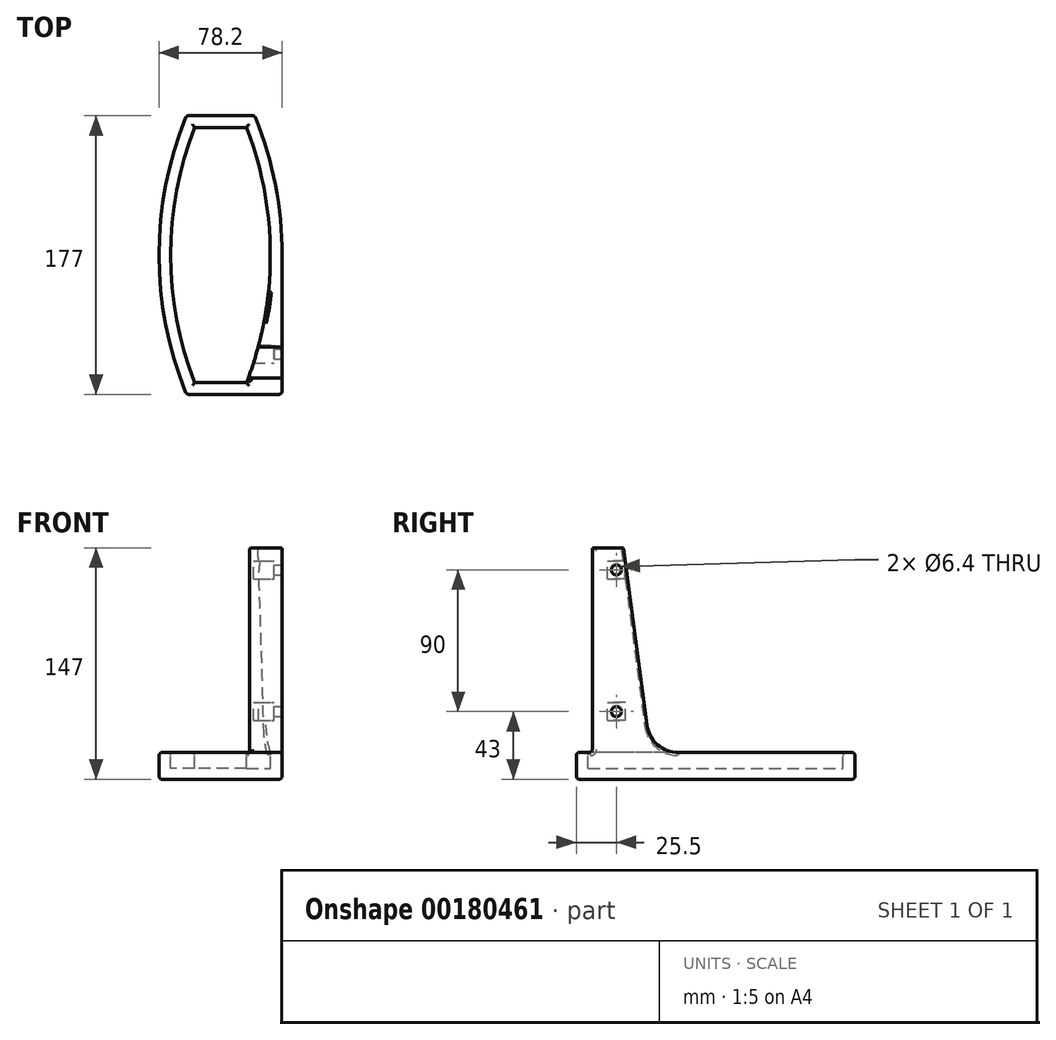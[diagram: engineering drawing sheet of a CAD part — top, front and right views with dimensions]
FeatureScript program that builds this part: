
annotation { "Feature Type Name" : "Feature", "Feature Type Description" : "" }
export const myFeature = defineFeature(function(context is Context, id is Id, definition is map)
    precondition{}
    {
        {
            var Q0;
            Q0=qCreatedBy(makeId("Top.planeOp"),FACE);
            var sketch = newSketch(context, id + "F0", { "sketchPlane" : qUnion([Q0])});
            skLineSegment(sketch, "E0.bottom", {"start": v(16.5, -81) * mm, "end": v(-16.5, -81) * mm});
            skLineSegment(sketch, "E0.top", {"start": v(16.5, 81) * mm, "end": v(-16.5, 81) * mm});
            skLineSegment(sketch, "E0.left", {"start": v(16.5, -81) * mm, "end": v(16.5, 81) * mm, "construction": true});
            skLineSegment(sketch, "E0.right", {"start": v(-16.5, -81) * mm, "end": v(-16.5, 81) * mm, "construction": true});
            skPoint(sketch, "E0.middle", {"position": v(0, 0) * mm});
            skArc(sketch, "E1", {"start": v(16.5, -81) * mm, "mid": v(31.6, 0) * mm, "end": v(16.5, 81) * mm});
            skArc(sketch, "E2", {"start": v(-16.5, 81) * mm, "mid": v(-31.6, 0) * mm, "end": v(-16.5, -81) * mm});
            skLineSegment(sketch, "E3", {"start": v(-31.6, 0) * mm, "end": v(31.6, 0) * mm, "construction": true});
            skSolve(sketch);
        }
        {
            var Q0;
            Q0=makeQuery(id+"F0.imprint","IMPRINT",FACE,{"disambiguationData":[TD([[makeQuery(id+"F0.imprint","IMPRINT",EDGE,{"derivedFrom":sQuery(id+"F0.wireOp",EDGE,"E0.bottom")}),-1.0]])]});
            var sketch = newSketch(context, id + "F1", { "sketchPlane" : qUnion([Q0])});
            skLineSegment(sketch, "E4.0", {"start": v(16.84, -81.5) * mm, "end": v(-16.84, -81.5) * mm});
            skArc(sketch, "E4.1", {"start": v(16.84, -81.5) * mm, "mid": v(32.1, 0) * mm, "end": v(16.84, 81.5) * mm});
            skLineSegment(sketch, "E4.2", {"start": v(16.84, 81.5) * mm, "end": v(-16.84, 81.5) * mm});
            skArc(sketch, "E4.3", {"start": v(-16.84, 81.5) * mm, "mid": v(-32.1, 0) * mm, "end": v(-16.84, -81.5) * mm});
            skLineSegment(sketch, "E5.0", {"start": v(-21.49, -88.5) * mm, "end": v(-21.58, -88.5) * mm});
            skArc(sketch, "E5.1", {"start": v(-21.58, 88.5) * mm, "mid": v(-39.1, 0) * mm, "end": v(-21.58, -88.5) * mm});
            skLineSegment(sketch, "E5.2", {"start": v(21.58, 88.5) * mm, "end": v(-21.58, 88.5) * mm});
            skLineSegment(sketch, "E6", {"start": v(21.58, 88.5) * mm, "end": v(21.58, 88.5) * mm});
            skLineSegment(sketch, "E7", {"start": v(39.1, 0) * mm, "end": v(39.1, -88.5) * mm});
            skLineSegment(sketch, "E8", {"start": v(39.1, -88.5) * mm, "end": v(-21.49, -88.5) * mm});
            skPoint(sketch, "E9", {"position": v(39.1, 0) * mm});
            skArc(sketch, "E10.0", {"start": v(39.1, 0) * mm, "mid": v(34.68, 45.1) * mm, "end": v(21.58, 88.5) * mm});
            skPoint(sketch, "E11.orphan", {"position": v(39.1, 88.5) * mm});
            skSolve(sketch);
        }
        {
            var Q0;
            Q0=makeQuery(id+"F0.imprint","IMPRINT",FACE,{"disambiguationData":[TD([[makeQuery(id+"F0.imprint","IMPRINT",EDGE,{"derivedFrom":sQuery(id+"F0.wireOp",EDGE,"E0.bottom")}),-1.0]])]});
            var Q1;
            Q1=makeQuery(id+"F1.imprint","IMPRINT",FACE,{"disambiguationData":[TD([[makeQuery(id+"F1.imprint","IMPRINT",EDGE,{"derivedFrom":sQuery(id+"F1.wireOp",EDGE,"E4.0")}),1.0]])]});
            var Q2;
            Q2=makeQuery(id+"F1.imprint","IMPRINT",FACE,{"disambiguationData":[TD([[makeQuery(id+"F1.imprint","IMPRINT",EDGE,{"derivedFrom":sQuery(id+"F1.wireOp",EDGE,"E4.0")}),-1.0]])]});
            extrude(context, id + "F2", {"entities" : qUnion([Q0, Q1, Q2]), "oppositeDirection" : true, "depth" : 7 * mm});
        }
        {
            var Q0;
            Q0=makeQuery(id+"F2.opExtrude","CAP_FACE",FACE,{"disambiguationData":[OSD([sQuery(id+"F1.wireOp",EDGE,"E4.0"),sQuery(id+"F1.wireOp",EDGE,"E4.1"),sQuery(id+"F1.wireOp",EDGE,"E4.2"),sQuery(id+"F1.wireOp",EDGE,"E4.3"),sQuery(id+"F1.wireOp",EDGE,"E5.1"),sQuery(id+"F1.wireOp",EDGE,"E5.2"),sQuery(id+"F1.wireOp",EDGE,"E7"),sQuery(id+"F1.wireOp",EDGE,"E8"),sQuery(id+"F1.wireOp",EDGE,"E10.0")])],"isStart":true});
            extrude(context, id + "F3", {"entities" : qUnion([Q0]), "operationType" : NewBodyOperationType.ADD, "depth" : 10 * mm});
        }
        {
            var Q0;
            Q0=makeQuery(id+"F3.opExtrude","CAP_FACE",FACE,{"disambiguationData":[OSD([sQuery(id+"F1.wireOp",EDGE,"E4.0"),sQuery(id+"F1.wireOp",EDGE,"E4.1"),sQuery(id+"F1.wireOp",EDGE,"E4.2"),sQuery(id+"F1.wireOp",EDGE,"E4.3"),sQuery(id+"F1.wireOp",EDGE,"E5.1"),sQuery(id+"F1.wireOp",EDGE,"E5.2"),sQuery(id+"F1.wireOp",EDGE,"E7"),sQuery(id+"F1.wireOp",EDGE,"E8"),sQuery(id+"F1.wireOp",EDGE,"E10.0")])],"isStart":false});
            var sketch = newSketch(context, id + "F4", { "sketchPlane" : qUnion([Q0])});
            skArc(sketch, "E12", {"start": v(13.45, -88.5) * mm, "mid": v(31.6, 0) * mm, "end": v(13.45, 88.5) * mm});
            skLineSegment(sketch, "E13.0", {"start": v(39.1, -88.5) * mm, "end": v(-21.58, -88.5) * mm, "construction": true});
            skLineSegment(sketch, "E13.1", {"start": v(21.58, 88.5) * mm, "end": v(-21.58, 88.5) * mm, "construction": true});
            skArc(sketch, "E14.0", {"start": v(39.1, 0) * mm, "mid": v(34.68, 45.1) * mm, "end": v(21.58, 88.5) * mm});
            skLineSegment(sketch, "E14.1", {"start": v(39.1, 0) * mm, "end": v(39.1, -88.5) * mm});
            skArc(sketch, "E15.0", {"start": v(16.5, -81) * mm, "mid": v(31.6, 0) * mm, "end": v(16.5, 81) * mm, "construction": true});
            skSolve(sketch);
        }
        {
            var Q0;
            Q0 = qSketchRegion(id + "F4", true);
            var Q1;
            {var subQ0=sQuery(id+"F4.wireOp",EDGE,"E14.0");Q1=makeQuery(id+"F4.imprint","IMPRINT",FACE,{"disambiguationData":[TD([[makeQuery(id+"F4.imprint","IMPRINT",EDGE,{"derivedFrom":subQ0}),1.0]])]});}
            extrude(context, id + "F5", {"entities" : qUnion([Q0, Q1]), "operationType" : NewBodyOperationType.ADD, "depth" : 130 * mm});
        }
        {
            var Q0;
            {var subQ0=sQuery(id+"F1.wireOp",EDGE,"E7");Q0=makeQuery(id+"FOVQ2Oselk7mZ5l_2.boolean.opBoolean","MERGE",FACE,{"derivedFrom":[makeQuery(id+"F5.boolean.opBoolean","MERGE",FACE,{"derivedFrom":[makeQuery(id+"F3.boolean.opBoolean","MERGE",FACE,{"derivedFrom":[makeQuery(id+"F2.opExtrude","SWEPT_FACE",FACE,{"disambiguationData":[OSD([subQ0])]}),makeQuery(id+"F3.opExtrude","SWEPT_FACE",FACE,{"disambiguationData":[OSD([subQ0])]})]}),makeQuery(id+"F5.opExtrude","SWEPT_FACE",FACE,{"disambiguationData":[OSD([sQuery(id+"F4.wireOp",EDGE,"E14.1")])]})]}),makeQuery(id+"FOVQ2Oselk7mZ5l_2.opExtrude","SWEPT_FACE",FACE,{"disambiguationData":[OSD([sQuery(id+"F3JGxH3bIZVlt3g_2.wireOp",EDGE,"1KpfjM26-rjeJ-PBDq-QVvU-KJFUgXuMp7k0.left")])]}),makeQuery(id+"FOVQ2Oselk7mZ5l_2.opExtrude","SWEPT_FACE",FACE,{"disambiguationData":[OSD([sQuery(id+"F3JGxH3bIZVlt3g_2.wireOp",EDGE,"XWPlUdq5-mJ3b-vQc1-ytmF-66MxpVRaScVq.left")])]})]});}
            var sketch = newSketch(context, id + "F6", { "sketchPlane" : qUnion([Q0])});
            skLineSegment(sketch, "E16.0", {"start": v(88.5, 10) * mm, "end": v(-23.68, 10) * mm, "construction": true});
            skLineSegment(sketch, "E17.bottom", {"start": v(-88.5, 140) * mm, "end": v(-58.5, 140) * mm});
            skLineSegment(sketch, "E17.top", {"start": v(-88.5, 10) * mm, "end": v(-49.42, 10) * mm});
            skLineSegment(sketch, "E17.left", {"start": v(-88.5, 140) * mm, "end": v(-88.5, 10) * mm});
            skLineSegment(sketch, "E17.right", {"start": v(-58.5, 140) * mm, "end": v(-43.5, 27.36) * mm});
            skLineSegment(sketch, "E18", {"start": v(-49.42, 10) * mm, "end": v(88.5, 10) * mm});
            skPoint(sketch, "E19.newPointB", {"position": v(-88.5, 10) * mm});
            skArc(sketch, "E19.filletArc", {"start": v(-43.5, 27.36) * mm, "mid": v(-36.85, 14.95) * mm, "end": v(-23.68, 10) * mm});
            skLineSegment(sketch, "E20", {"start": v(-58.5, 140) * mm, "end": v(88.5, 140.05) * mm});
            skLineSegment(sketch, "E21", {"start": v(88.5, 140.05) * mm, "end": v(88.5, 10) * mm});
            skSolve(sketch);
        }
        {
            var Q0;
            {var subQ0=sQuery(id+"F6.wireOp",EDGE,"E17.right");Q0=makeQuery(id+"F6.imprint","IMPRINT",FACE,{"disambiguationData":[TD([[makeQuery(id+"F6.imprint","IMPRINT",EDGE,{"derivedFrom":subQ0}),1.0]])]});}
            var Q1;
            {var subQ5=sQuery(id+"F6.wireOp",EDGE,"E21");Q1=makeQuery(id+"F6.imprint","IMPRINT",FACE,{"disambiguationData":[TD([[makeQuery(id+"F6.imprint","IMPRINT",EDGE,{"derivedFrom":subQ5}),-1.0]])]});}
            var Q2;
            {var subQ0=sQuery(id+"F0.wireOp",EDGE,"E2");Q2=makeQuery(id+"F3.boolean.opBoolean","MERGE",FACE,{"derivedFrom":[makeQuery(id+"F2.opExtrude","SWEPT_FACE",FACE,{"disambiguationData":[OSD([subQ0]),TDD([makeQuery(id+"F1.imprint","IMPRINT",EDGE,{"derivedFrom":makeQuery(id+"F0.imprint","IMPRINT",EDGE,{"derivedFrom":subQ0})})])]}),makeQuery(id+"F3.opExtrude","SWEPT_FACE",FACE,{"disambiguationData":[OSD([subQ0])]})]});}
            extrude(context, id + "F7", {"entities" : qUnion([Q0, Q1]), "operationType" : NewBodyOperationType.REMOVE, "endBound" : BoundingType.UP_TO_SURFACE, "oppositeDirection" : true, "endBoundEntityFace" : qUnion([Q2]), "depth" : 25 * mm});
        }
        {
            var Q0;
            {var subQ0=sQuery(id+"F1.wireOp",EDGE,"E7");Q0=makeQuery(id+"FOVQ2Oselk7mZ5l_2.boolean.opBoolean","MERGE",FACE,{"derivedFrom":[makeQuery(id+"F5.boolean.opBoolean","MERGE",FACE,{"derivedFrom":[makeQuery(id+"F3.boolean.opBoolean","MERGE",FACE,{"derivedFrom":[makeQuery(id+"F2.opExtrude","SWEPT_FACE",FACE,{"disambiguationData":[OSD([subQ0])]}),makeQuery(id+"F3.opExtrude","SWEPT_FACE",FACE,{"disambiguationData":[OSD([subQ0])]})]}),makeQuery(id+"F5.opExtrude","SWEPT_FACE",FACE,{"disambiguationData":[OSD([sQuery(id+"F4.wireOp",EDGE,"E14.1")])]})]}),makeQuery(id+"FOVQ2Oselk7mZ5l_2.opExtrude","SWEPT_FACE",FACE,{"disambiguationData":[OSD([sQuery(id+"F3JGxH3bIZVlt3g_2.wireOp",EDGE,"1KpfjM26-rjeJ-PBDq-QVvU-KJFUgXuMp7k0.left")])]}),makeQuery(id+"FOVQ2Oselk7mZ5l_2.opExtrude","SWEPT_FACE",FACE,{"disambiguationData":[OSD([sQuery(id+"F3JGxH3bIZVlt3g_2.wireOp",EDGE,"XWPlUdq5-mJ3b-vQc1-ytmF-66MxpVRaScVq.left")])]})]});}
            var sketch = newSketch(context, id + "F8", { "sketchPlane" : qUnion([Q0])});
            skPoint(sketch, "E22.0", {"position": v(-88.5, 10) * mm});
            skPoint(sketch, "E22.1", {"position": v(-81, 10) * mm});
            skLineSegment(sketch, "E23.bottom", {"start": v(-80.3, 10) * mm, "end": v(-88.5, 10) * mm});
            skLineSegment(sketch, "E23.top", {"start": v(-78.3, 140) * mm, "end": v(-88.5, 140) * mm});
            skLineSegment(sketch, "E23.left", {"start": v(-78.3, 12) * mm, "end": v(-78.3, 140) * mm});
            skLineSegment(sketch, "E23.right", {"start": v(-88.5, 10) * mm, "end": v(-88.5, 140) * mm});
            skPoint(sketch, "E24.visualSharp", {"position": v(-78.3, 10) * mm});
            skArc(sketch, "E24.filletArc", {"start": v(-80.3, 10) * mm, "mid": v(-78.89, 10.59) * mm, "end": v(-78.3, 12) * mm});
            skSolve(sketch);
        }
        {
            var Q0;
            Q0=makeQuery(id+"F8.imprint","IMPRINT",FACE,{"disambiguationData":[TD([[makeQuery(id+"F8.imprint","IMPRINT",EDGE,{"derivedFrom":sQuery(id+"F8.wireOp",EDGE,"E23.bottom")}),-1.0]])]});
            extrude(context, id + "F9", {"entities" : qUnion([Q0]), "operationType" : NewBodyOperationType.REMOVE, "endBound" : BoundingType.THROUGH_ALL, "oppositeDirection" : true, "depth" : 25 * mm});
        }
        {
            var Q0;
            Q0=makeQuery(id+"F3.opExtrude","CAP_EDGE",EDGE,{"disambiguationData":[OSD([sQuery(id+"F0.wireOp",EDGE,"E0.top")])],"isStart":false});
            var Q1;
            {var subQ0=sQuery(id+"F0.wireOp",EDGE,"E1");Q1=makeQuery(id+"F7.boolean.opBoolean","INTERSECT",EDGE,{"derivedFrom":[makeQuery(id+"F5.boolean.opBoolean","MERGE",FACE,{"derivedFrom":[makeQuery(id+"F3.boolean.opBoolean","MERGE",FACE,{"derivedFrom":[makeQuery(id+"F2.opExtrude","SWEPT_FACE",FACE,{"disambiguationData":[OSD([subQ0]),TDD([makeQuery(id+"F1.imprint","IMPRINT",EDGE,{"derivedFrom":makeQuery(id+"F0.imprint","IMPRINT",EDGE,{"derivedFrom":subQ0})})])]}),makeQuery(id+"F3.opExtrude","SWEPT_FACE",FACE,{"disambiguationData":[OSD([subQ0])]})]}),makeQuery(id+"F5.opExtrude","SWEPT_FACE",FACE,{"disambiguationData":[OSD([sQuery(id+"F4.wireOp",EDGE,"E12")])]})]}),makeQuery(id+"F7.opExtrude","SWEPT_FACE",FACE,{"disambiguationData":[OSD([sQuery(id+"F6.wireOp",EDGE,"E18")])]})]});}
            var Q2;
            Q2=makeQuery(id+"F5.opExtrude","CAP_EDGE",EDGE,{"disambiguationData":[OSD([sQuery(id+"F4.wireOp",EDGE,"E12")])],"isStart":false});
            var Q3;
            {var subQ0=sQuery(id+"F0.wireOp",EDGE,"E1");Q3=makeQuery(id+"F9.boolean.opBoolean","INTERSECT",EDGE,{"derivedFrom":[makeQuery(id+"F5.boolean.opBoolean","MERGE",FACE,{"derivedFrom":[makeQuery(id+"F3.boolean.opBoolean","MERGE",FACE,{"derivedFrom":[makeQuery(id+"F2.opExtrude","SWEPT_FACE",FACE,{"disambiguationData":[OSD([subQ0]),TDD([makeQuery(id+"F1.imprint","IMPRINT",EDGE,{"derivedFrom":makeQuery(id+"F0.imprint","IMPRINT",EDGE,{"derivedFrom":subQ0})})])]}),makeQuery(id+"F3.opExtrude","SWEPT_FACE",FACE,{"disambiguationData":[OSD([subQ0])]})]}),makeQuery(id+"F5.opExtrude","SWEPT_FACE",FACE,{"disambiguationData":[OSD([sQuery(id+"F4.wireOp",EDGE,"E12")])]})]}),makeQuery(id+"F9.opExtrude","SWEPT_FACE",FACE,{"disambiguationData":[OSD([sQuery(id+"F8.wireOp",EDGE,"E23.left")])]})]});}
            var Q4;
            Q4=makeQuery(id+"F3.opExtrude","CAP_EDGE",EDGE,{"disambiguationData":[OSD([sQuery(id+"F0.wireOp",EDGE,"E0.bottom")])],"isStart":false});
            var Q5;
            Q5=makeQuery(id+"F3.opExtrude","CAP_EDGE",EDGE,{"disambiguationData":[OSD([sQuery(id+"F0.wireOp",EDGE,"E2")])],"isStart":false});
            var Q6;
            Q6=makeQuery(id+"F9.boolean.opBoolean","COPY",EDGE,{"derivedFrom":makeQuery(id+"F9.opExtrude","SWEPT_EDGE",EDGE,{"disambiguationData":[OSD([sQuery(id+"F4.wireOp",EDGE,"E14.1"),sQuery(id+"F8.wireOp",EDGE,"E23.top"),sQuery(id+"F8.wireOp",EDGE,"E23.left")])]})});
            var Q7;
            Q7=makeQuery(id+"F7.boolean.opBoolean","COPY",EDGE,{"derivedFrom":makeQuery(id+"F7.opExtrude","SWEPT_EDGE",EDGE,{"disambiguationData":[OSD([sQuery(id+"F6.wireOp",EDGE,"E17.bottom"),sQuery(id+"F6.wireOp",EDGE,"E17.right"),sQuery(id+"F6.wireOp",EDGE,"E20")])]})});
            var Q8;
            {var subQ0=sQuery(id+"F1.wireOp",EDGE,"E8");var subQ1=sQuery(id+"F1.wireOp",EDGE,"E5.1");Q8=makeQuery(id+"F3.boolean.opBoolean","MERGE",EDGE,{"derivedFrom":[makeQuery(id+"F2.opExtrude","SWEPT_EDGE",EDGE,{"disambiguationData":[OSD([subQ1,subQ0])]}),makeQuery(id+"F3.opExtrude","SWEPT_EDGE",EDGE,{"disambiguationData":[OSD([subQ1,subQ0])]})]});}
            var Q9;
            {var subQ0=sQuery(id+"F1.wireOp",EDGE,"E5.2");var subQ1=sQuery(id+"F1.wireOp",EDGE,"E10.0");Q9=makeQuery(id+"F5.boolean.opBoolean","MERGE",EDGE,{"derivedFrom":[makeQuery(id+"F3.boolean.opBoolean","MERGE",EDGE,{"derivedFrom":[makeQuery(id+"F2.opExtrude","SWEPT_EDGE",EDGE,{"disambiguationData":[OSD([subQ0,subQ1])]}),makeQuery(id+"F3.opExtrude","SWEPT_EDGE",EDGE,{"disambiguationData":[OSD([subQ0,subQ1])]})]}),makeQuery(id+"F5.opExtrude","SWEPT_EDGE",EDGE,{"disambiguationData":[OSD([subQ0,sQuery(id+"F4.wireOp",EDGE,"E14.0")])]})]});}
            var Q10;
            {var subQ0=sQuery(id+"F1.wireOp",EDGE,"E5.2");var subQ1=sQuery(id+"F1.wireOp",EDGE,"E5.1");Q10=makeQuery(id+"F3.boolean.opBoolean","MERGE",EDGE,{"derivedFrom":[makeQuery(id+"F2.opExtrude","SWEPT_EDGE",EDGE,{"disambiguationData":[OSD([subQ1,subQ0])]}),makeQuery(id+"F3.opExtrude","SWEPT_EDGE",EDGE,{"disambiguationData":[OSD([subQ1,subQ0])]})]});}
            var Q11;
            Q11=makeQuery(id+"F9.boolean.opBoolean","MERGE",FACE,{"derivedFrom":[makeQuery(id+"F7.boolean.opBoolean","MERGE",FACE,{"derivedFrom":[makeQuery(id+"F3.opExtrude","CAP_FACE",FACE,{"disambiguationData":[OSD([sQuery(id+"F0.wireOp",EDGE,"E0.bottom"),sQuery(id+"F0.wireOp",EDGE,"E0.top"),sQuery(id+"F0.wireOp",EDGE,"E1"),sQuery(id+"F0.wireOp",EDGE,"E2"),sQuery(id+"F1.wireOp",EDGE,"E5.1"),sQuery(id+"F1.wireOp",EDGE,"E5.2"),sQuery(id+"F1.wireOp",EDGE,"E7"),sQuery(id+"F1.wireOp",EDGE,"E8"),sQuery(id+"F1.wireOp",EDGE,"E10.0")])],"isStart":false}),makeQuery(id+"F7.opExtrude","SWEPT_FACE",FACE,{"disambiguationData":[OSD([sQuery(id+"F6.wireOp",EDGE,"E18")])]})]}),makeQuery(id+"F9.opExtrude","SWEPT_FACE",FACE,{"disambiguationData":[OSD([sQuery(id+"F8.wireOp",EDGE,"E23.bottom")])]})]});
            var Q12;
            Q12=makeQuery(id+"F2.opExtrude","CAP_EDGE",EDGE,{"disambiguationData":[OSD([sQuery(id+"F1.wireOp",EDGE,"E8")])],"isStart":false});
            var Q13;
            Q13=makeQuery(id+"F2.opExtrude","CAP_EDGE",EDGE,{"disambiguationData":[OSD([sQuery(id+"F1.wireOp",EDGE,"E5.1")])],"isStart":false});
            var Q14;
            Q14=makeQuery(id+"F2.opExtrude","CAP_EDGE",EDGE,{"disambiguationData":[OSD([sQuery(id+"F1.wireOp",EDGE,"E5.2")])],"isStart":false});
            var Q15;
            Q15=makeQuery(id+"F2.opExtrude","CAP_EDGE",EDGE,{"disambiguationData":[OSD([sQuery(id+"F1.wireOp",EDGE,"E10.0")])],"isStart":false});
            fillet(context, id + "F10", {"entities" : qUnion([Q0, Q1, Q2, Q3, Q4, Q5, Q6, Q7, Q8, Q9, Q10, Q11, Q12, Q13, Q14, Q15]), "radius" : 2 * mm, "tangentPropagation" : true, "allowEdgeOverflow" : false});
        }
        {
            var Q0;
            {var subQ0=sQuery(id+"F1.wireOp",EDGE,"E7");Q0=makeQuery(id+"F5.boolean.opBoolean","MERGE",FACE,{"derivedFrom":[makeQuery(id+"F3.boolean.opBoolean","MERGE",FACE,{"derivedFrom":[makeQuery(id+"F2.opExtrude","SWEPT_FACE",FACE,{"disambiguationData":[OSD([subQ0])]}),makeQuery(id+"F3.opExtrude","SWEPT_FACE",FACE,{"disambiguationData":[OSD([subQ0])]})]}),makeQuery(id+"F5.opExtrude","SWEPT_FACE",FACE,{"disambiguationData":[OSD([sQuery(id+"F4.wireOp",EDGE,"E14.1")])]})]});}
            var sketch = newSketch(context, id + "F11", { "sketchPlane" : qUnion([Q0])});
            skPoint(sketch, "E25", {"position": v(-63, 36) * mm});
            skPoint(sketch, "E26", {"position": v(-63, 126) * mm});
            skSolve(sketch);
        }
        {
            var Q0;
            Q0=sQuery(id+"F11.wireOp",VERTEX,"E26");
            var Q1;
            Q1=sQuery(id+"F11.wireOp",VERTEX,"E25");
            var Q2;
            Q2=makeQuery(id+"F2.opExtrude","SWEPT_BODY",BODY,{"disambiguationData":[OSD([sQuery(id+"F0.wireOp",EDGE,"E0.bottom"),sQuery(id+"F0.wireOp",EDGE,"E0.top"),sQuery(id+"F0.wireOp",EDGE,"E1"),sQuery(id+"F0.wireOp",EDGE,"E2")])]});
            hole(context, id + "F12", {"style" : HoleStyle.SIMPLE, "endStyle" : HoleEndStyle.THROUGH, "holeDiameter" : 6.4 * mm, "locations" : qUnion([Q0, Q1]), "scope" : qUnion([Q2]), "isTappedThrough" : true});
        }
        {
            var Q0;
            {var subQ0=sQuery(id+"F1.wireOp",EDGE,"E7");Q0=makeQuery(id+"F5.boolean.opBoolean","MERGE",FACE,{"derivedFrom":[makeQuery(id+"F3.boolean.opBoolean","MERGE",FACE,{"derivedFrom":[makeQuery(id+"F2.opExtrude","SWEPT_FACE",FACE,{"disambiguationData":[OSD([subQ0])]}),makeQuery(id+"F3.opExtrude","SWEPT_FACE",FACE,{"disambiguationData":[OSD([subQ0])]})]}),makeQuery(id+"F5.opExtrude","SWEPT_FACE",FACE,{"disambiguationData":[OSD([sQuery(id+"F4.wireOp",EDGE,"E14.1")])]})]});}
            cPlane(context, id + "F13", {"entities" : qUnion([Q0]), "cplaneType" : CPlaneType.OFFSET, "offset" : 5 * mm, "oppositeDirection" : true, "width" : 150 * mm, "height" : 150 * mm});
        }
        {
            var Q0;
            Q0=qCreatedBy(id+"F13.planeOp",FACE);
            var sketch = newSketch(context, id + "F14", { "sketchPlane" : qUnion([Q0])});
            skLineSegment(sketch, "E27.bottom", {"start": v(-57.4, 120.3) * mm, "end": v(-68.6, 120.3) * mm});
            skLineSegment(sketch, "E27.top", {"start": v(-57.4, 131.7) * mm, "end": v(-68.6, 131.7) * mm});
            skLineSegment(sketch, "E27.left", {"start": v(-57.4, 120.3) * mm, "end": v(-57.4, 131.7) * mm});
            skLineSegment(sketch, "E27.right", {"start": v(-68.6, 120.3) * mm, "end": v(-68.6, 131.7) * mm});
            skPoint(sketch, "E27.middle", {"position": v(-63, 126) * mm});
            skLineSegment(sketch, "E28.bottom", {"start": v(-57.3, 30.3) * mm, "end": v(-68.7, 30.3) * mm});
            skLineSegment(sketch, "E28.top", {"start": v(-57.3, 41.7) * mm, "end": v(-68.7, 41.7) * mm});
            skLineSegment(sketch, "E28.left", {"start": v(-57.3, 30.3) * mm, "end": v(-57.3, 41.7) * mm});
            skLineSegment(sketch, "E28.right", {"start": v(-68.7, 30.3) * mm, "end": v(-68.7, 41.7) * mm});
            skPoint(sketch, "E28.middle", {"position": v(-63, 36) * mm});
            skSolve(sketch);
        }
        {
            var Q0;
            Q0=makeQuery(id+"F14.imprint","IMPRINT",FACE,{"disambiguationData":[TD([[makeQuery(id+"F14.imprint","IMPRINT",EDGE,{"derivedFrom":sQuery(id+"F14.wireOp",EDGE,"E27.bottom")}),-1.0]])]});
            var Q1;
            Q1=makeQuery(id+"F14.imprint","IMPRINT",FACE,{"disambiguationData":[TD([[makeQuery(id+"F14.imprint","IMPRINT",EDGE,{"derivedFrom":sQuery(id+"F14.wireOp",EDGE,"E28.bottom")}),-1.0]])]});
            extrude(context, id + "F15", {"entities" : qUnion([Q0, Q1]), "operationType" : NewBodyOperationType.REMOVE, "oppositeDirection" : true, "depth" : 25 * mm});
        }
    });
